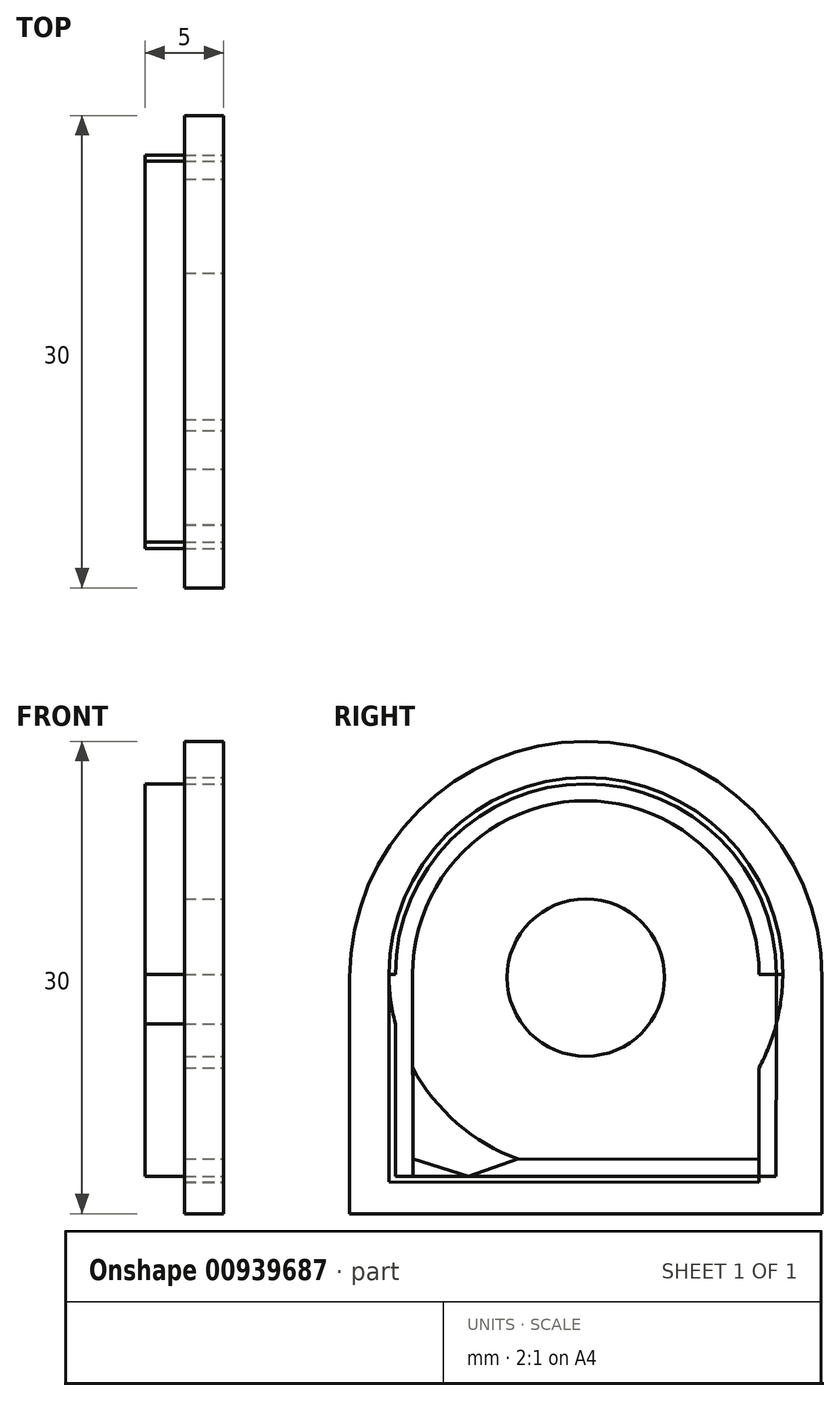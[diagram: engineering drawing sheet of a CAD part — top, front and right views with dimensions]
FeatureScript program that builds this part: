
annotation { "Feature Type Name" : "Feature", "Feature Type Description" : "" }
export const myFeature = defineFeature(function(context is Context, id is Id, definition is map)
    precondition{}
    {
        {
            var Q0;
            Q0=qCreatedBy(makeId("Right.planeOp"),FACE);
            var sketch = newSketch(context, id + "F0", { "sketchPlane" : qUnion([Q0])});
            skArc(sketch, "E0.0", {"start": v(-0.62, 5.76) * mm, "mid": v(-13.12, 18.27) * mm, "end": v(-25.63, 5.77) * mm});
            skArc(sketch, "E1.0", {"start": v(1.88, 5.56) * mm, "mid": v(-13.13, 20.56) * mm, "end": v(-28.12, 5.56) * mm});
            skLineSegment(sketch, "E2.0.0", {"start": v(-28.12, -9.44) * mm, "end": v(1.88, -9.44) * mm});
            skLineSegment(sketch, "E2.0.1", {"start": v(1.88, -9.44) * mm, "end": v(1.88, -4.44) * mm});
            skLineSegment(sketch, "E2.0.2", {"start": v(1.88, -4.44) * mm, "end": v(1.88, 5.56) * mm});
            skLineSegment(sketch, "E2.0.4", {"start": v(-28.12, 5.56) * mm, "end": v(-28.12, -9.44) * mm});
            skLineSegment(sketch, "E3.0", {"start": v(-25.63, 5.77) * mm, "end": v(-25.63, -7.44) * mm});
            skLineSegment(sketch, "E4.0", {"start": v(-25.63, -7.44) * mm, "end": v(-0.62, -7.44) * mm});
            skLineSegment(sketch, "E5.0", {"start": v(-0.62, 5.76) * mm, "end": v(-0.62, -7.44) * mm});
            skLineSegment(sketch, "E6.0.0", {"start": v(1.88, -9.44) * mm, "end": v(71.88, -9.44) * mm});
            skLineSegment(sketch, "E6.0.1", {"start": v(71.88, -9.44) * mm, "end": v(66.88, -4.44) * mm});
            skLineSegment(sketch, "E6.0.2", {"start": v(66.88, -4.44) * mm, "end": v(1.88, -4.44) * mm});
            skLineSegment(sketch, "E6.0.3", {"start": v(1.88, -4.44) * mm, "end": v(1.88, -9.44) * mm});
            skCircle(sketch, "E7", {"center": v(-13.12, 5.76) * mm, "radius": 12.5 * mm});
            skCircle(sketch, "E8", {"center": v(-13.12, 5.56) * mm, "radius": 5 * mm});
            skLineSegment(sketch, "E9", {"start": v(-25.63, 5.77) * mm, "end": v(-24.13, 5.77) * mm});
            skLineSegment(sketch, "E10", {"start": v(-0.62, 5.76) * mm, "end": v(-2.12, 5.76) * mm});
            skArc(sketch, "E11", {"start": v(-2.12, 5.76) * mm, "mid": v(-13.12, 16.79) * mm, "end": v(-24.13, 5.77) * mm});
            skLineSegment(sketch, "E12", {"start": v(-0.62, 5.76) * mm, "end": v(-1.02, 5.76) * mm});
            skLineSegment(sketch, "E13", {"start": v(-25.63, 5.77) * mm, "end": v(-25.23, 5.77) * mm});
            skArc(sketch, "E14", {"start": v(-1.02, 5.76) * mm, "mid": v(-13.12, 17.87) * mm, "end": v(-25.23, 5.77) * mm});
            skLineSegment(sketch, "E15", {"start": v(-25.23, 5.77) * mm, "end": v(-25.23, -7.44) * mm});
            skLineSegment(sketch, "E16", {"start": v(-24.13, 5.77) * mm, "end": v(-24.1, -7.44) * mm});
            skLineSegment(sketch, "E17", {"start": v(-2.12, 5.76) * mm, "end": v(-2.15, -7.44) * mm});
            skLineSegment(sketch, "E18", {"start": v(-1.02, 5.76) * mm, "end": v(-1.05, -7.44) * mm});
            skLineSegment(sketch, "E19", {"start": v(-1.05, -7.44) * mm, "end": v(-24.1, -7.44) * mm});
            skLineSegment(sketch, "E20", {"start": v(-24.1, -7.44) * mm, "end": v(-24.1, -7.04) * mm});
            skLineSegment(sketch, "E21", {"start": v(-2.15, -7.08) * mm, "end": v(-2.14, -5.98) * mm});
            skLineSegment(sketch, "E22", {"start": v(-2.14, -5.98) * mm, "end": v(-24.1, -5.97) * mm});
            skLineSegment(sketch, "E23", {"start": v(-24.1, -5.97) * mm, "end": v(-17.43, -5.97) * mm});
            skLineSegment(sketch, "E24", {"start": v(-8.83, -5.98) * mm, "end": v(-2.14, -5.98) * mm});
            skLineSegment(sketch, "E25", {"start": v(-2.15, -7.08) * mm, "end": v(-1.05, -7.08) * mm});
            skLineSegment(sketch, "E26", {"start": v(-1.05, -7.08) * mm, "end": v(-25.23, -7.07) * mm});
            skLineSegment(sketch, "E27", {"start": v(-17.43, -5.97) * mm, "end": v(-20.57, -7.07) * mm});
            skLineSegment(sketch, "E28", {"start": v(-20.57, -7.07) * mm, "end": v(-24.1, -5.97) * mm});
            skLineSegment(sketch, "E29", {"start": v(-24.1, -5.97) * mm, "end": v(-24.1, -7.04) * mm});
            skSolve(sketch);
        }
        {
            var Q0;
            Q0=makeQuery(id+"F0.imprint","IMPRINT",FACE,{"disambiguationData":[TD([[makeQuery(id+"F0.imprint","IMPRINT",EDGE,{"derivedFrom":sQuery(id+"F0.wireOp",EDGE,"E2.0.0")}),1.0]])]});
            var Q1;
            Q1=makeQuery(id+"F0.imprint","IMPRINT",FACE,{"disambiguationData":[TD([[makeQuery(id+"F0.imprint","IMPRINT",EDGE,{"derivedFrom":sQuery(id+"F0.wireOp",EDGE,"E8")}),-1.0]])]});
            var Q2;
            {var subQ0=sQuery(id+"F0.wireOp",EDGE,"E3.0");Q2=makeQuery(id+"F0.imprint","IMPRINT",FACE,{"disambiguationData":[TD([[makeQuery(id+"F0.imprint","IMPRINT",EDGE,{"derivedFrom":subQ0}),1.0]])]});}
            var Q3;
            Q3=makeQuery(id+"F0.imprint","IMPRINT",FACE,{"disambiguationData":[TD([[makeQuery(id+"F0.imprint","IMPRINT",EDGE,{"derivedFrom":sQuery(id+"F0.wireOp",EDGE,"E9")}),1.0]])]});
            var Q4;
            {var subQ0=sQuery(id+"F0.wireOp",EDGE,"E12");Q4=makeQuery(id+"F0.imprint","IMPRINT",FACE,{"disambiguationData":[TD([[makeQuery(id+"F0.imprint","IMPRINT",EDGE,{"derivedFrom":subQ0}),-1.0]])]});}
            var Q5;
            {var subQ2=sQuery(id+"F0.wireOp",EDGE,"E13");Q5=makeQuery(id+"F0.imprint","IMPRINT",FACE,{"disambiguationData":[TD([[makeQuery(id+"F0.imprint","IMPRINT",EDGE,{"derivedFrom":subQ2}),-1.0]])]});}
            var Q6;
            {var subQ5=sQuery(id+"F0.wireOp",EDGE,"E9");Q6=makeQuery(id+"F0.imprint","IMPRINT",FACE,{"disambiguationData":[TD([[makeQuery(id+"F0.imprint","IMPRINT",EDGE,{"derivedFrom":subQ5}),-1.0]])]});}
            var Q7;
            {var subQ0=sQuery(id+"F0.wireOp",EDGE,"E20");Q7=makeQuery(id+"F0.imprint","IMPRINT",FACE,{"disambiguationData":[TD([[makeQuery(id+"F0.imprint","IMPRINT",EDGE,{"derivedFrom":subQ0}),1.0]])]});}
            var Q8;
            {var subQ0=sQuery(id+"F0.wireOp",EDGE,"NrDhrhhL-rTPf-8MJP-CKrF-6Iw7iG4QOgd4");Q8=makeQuery(id+"F0.imprint","IMPRINT",FACE,{"disambiguationData":[TD([[makeQuery(id+"F0.imprint","IMPRINT",EDGE,{"derivedFrom":subQ0}),1.0]])]});}
            var Q9;
            {var subQ0=sQuery(id+"F0.wireOp",EDGE,"E22");var subQ1=sQuery(id+"F0.wireOp",EDGE,"E7");var subQ2=makeQuery(id+"F0.imprint","INTERSECT",VERTEX,{"disambiguationData":[OD(0.0)],"derivedFrom":[subQ1,subQ0]});Q9=makeQuery(id+"F0.imprint","IMPRINT",FACE,{"disambiguationData":[TD([[makeQuery(id+"F0.imprint","IMPRINT",EDGE,{"disambiguationData":[TD([[subQ2,-1.0]])],"derivedFrom":subQ1}),1.0]])]});}
            var Q10;
            {var subQ3=sQuery(id+"F0.wireOp",EDGE,"E20");Q10=makeQuery(id+"F0.imprint","IMPRINT",FACE,{"disambiguationData":[TD([[makeQuery(id+"F0.imprint","IMPRINT",EDGE,{"derivedFrom":subQ3}),-1.0]])]});}
            var Q11;
            {var subQ0=sQuery(id+"F0.wireOp",EDGE,"E5.0");Q11=makeQuery(id+"F0.imprint","IMPRINT",FACE,{"disambiguationData":[TD([[makeQuery(id+"F0.imprint","IMPRINT",EDGE,{"derivedFrom":subQ0}),-1.0]])]});}
            var Q12;
            {var subQ0=sQuery(id+"F0.wireOp",EDGE,"E12");Q12=makeQuery(id+"F0.imprint","IMPRINT",FACE,{"disambiguationData":[TD([[makeQuery(id+"F0.imprint","IMPRINT",EDGE,{"derivedFrom":subQ0}),1.0]])]});}
            var Q13;
            {var subQ5=sQuery(id+"F0.wireOp",EDGE,"E10");Q13=makeQuery(id+"F0.imprint","IMPRINT",FACE,{"disambiguationData":[TD([[makeQuery(id+"F0.imprint","IMPRINT",EDGE,{"derivedFrom":subQ5}),1.0]])]});}
            var Q14;
            {var subQ3=sQuery(id+"F0.wireOp",EDGE,"E7");var subQ5=sQuery(id+"F0.wireOp",EDGE,"E17");var subQ8=makeQuery(id+"F0.imprint","INTERSECT",VERTEX,{"derivedFrom":[subQ3,subQ5]});Q14=makeQuery(id+"F0.imprint","IMPRINT",FACE,{"disambiguationData":[TD([[makeQuery(id+"F0.imprint","IMPRINT",EDGE,{"disambiguationData":[TD([[subQ8,-1.0]])],"derivedFrom":subQ3}),-1.0]])]});}
            var Q15;
            {var subQ0=sQuery(id+"F0.wireOp",EDGE,"E22");var subQ1=sQuery(id+"F0.wireOp",EDGE,"E7");var subQ2=makeQuery(id+"F0.imprint","INTERSECT",VERTEX,{"disambiguationData":[OD(1.0)],"derivedFrom":[subQ1,subQ0]});Q15=makeQuery(id+"F0.imprint","IMPRINT",FACE,{"disambiguationData":[TD([[makeQuery(id+"F0.imprint","IMPRINT",EDGE,{"disambiguationData":[TD([[subQ2,-1.0]])],"derivedFrom":subQ1}),-1.0]])]});}
            var Q16;
            {var subQ5=sQuery(id+"F0.wireOp",EDGE,"E7");var subQ7=sQuery(id+"F0.wireOp",EDGE,"E15");var subQ9=makeQuery(id+"F0.imprint","INTERSECT",VERTEX,{"derivedFrom":[subQ5,subQ7]});Q16=makeQuery(id+"F0.imprint","IMPRINT",FACE,{"disambiguationData":[TD([[makeQuery(id+"F0.imprint","IMPRINT",EDGE,{"disambiguationData":[TD([[subQ9,-1.0]])],"derivedFrom":subQ5}),-1.0]])]});}
            var Q17;
            {var subQ0=sQuery(id+"F0.wireOp",EDGE,"E24");Q17=makeQuery(id+"F0.imprint","IMPRINT",FACE,{"disambiguationData":[TD([[makeQuery(id+"F0.imprint","IMPRINT",EDGE,{"derivedFrom":subQ0}),1.0]])]});}
            var Q18;
            {var subQ2=sQuery(id+"F0.wireOp",EDGE,"E17");var subQ5=sQuery(id+"F0.wireOp",EDGE,"E19");var subQ8=makeQuery(id+"F0.imprint","INTERSECT",VERTEX,{"derivedFrom":[subQ2,subQ5]});Q18=makeQuery(id+"F0.imprint","IMPRINT",FACE,{"disambiguationData":[TD([[makeQuery(id+"F0.imprint","IMPRINT",EDGE,{"disambiguationData":[TD([[subQ8,1.0]])],"derivedFrom":subQ2}),-1.0]])]});}
            var Q19;
            {var subQ0=sQuery(id+"F0.wireOp",EDGE,"E19");var subQ1=sQuery(id+"F0.wireOp",EDGE,"E17");var subQ2=makeQuery(id+"F0.imprint","INTERSECT",VERTEX,{"derivedFrom":[subQ1,subQ0]});Q19=makeQuery(id+"F0.imprint","IMPRINT",FACE,{"disambiguationData":[TD([[makeQuery(id+"F0.imprint","IMPRINT",EDGE,{"disambiguationData":[TD([[subQ2,1.0]])],"derivedFrom":subQ1}),1.0]])]});}
            var Q20;
            {var subQ0=sQuery(id+"F0.wireOp",EDGE,"E23");Q20=makeQuery(id+"F0.imprint","IMPRINT",FACE,{"disambiguationData":[TD([[makeQuery(id+"F0.imprint","IMPRINT",EDGE,{"derivedFrom":subQ0}),1.0]])]});}
            var Q21;
            Q21=makeQuery(id+"F0.imprint","IMPRINT",FACE,{"disambiguationData":[TD([[makeQuery(id+"F0.imprint","IMPRINT",EDGE,{"derivedFrom":sQuery(id+"F0.wireOp",EDGE,"E23")}),-1.0]])]});
            var Q22;
            {var subQ1=sQuery(id+"F0.wireOp",EDGE,"E21");Q22=makeQuery(id+"F0.imprint","IMPRINT",FACE,{"disambiguationData":[TD([[makeQuery(id+"F0.imprint","IMPRINT",EDGE,{"derivedFrom":subQ1}),1.0]])]});}
            var Q23;
            {var subQ0=sQuery(id+"F0.wireOp",EDGE,"E22");Q23=makeQuery(id+"F0.imprint","IMPRINT",FACE,{"disambiguationData":[TD([[makeQuery(id+"F0.imprint","IMPRINT",EDGE,{"derivedFrom":subQ0}),1.0]])]});}
            extrude(context, id + "F1", {"entities" : qUnion([Q0, Q1, Q2, Q3, Q4, Q5, Q6, Q7, Q8, Q9, Q10, Q11, Q12, Q13, Q14, Q15, Q16, Q17, Q18, Q19, Q20, Q21, Q22, Q23]), "oppositeDirection" : true, "depth" : 2.5 * mm, "offsetDistance" : 25 * mm});
        }
        {
            var Q0;
            {var subQ5=sQuery(id+"F0.wireOp",EDGE,"E9");Q0=makeQuery(id+"F0.imprint","IMPRINT",FACE,{"disambiguationData":[TD([[makeQuery(id+"F0.imprint","IMPRINT",EDGE,{"derivedFrom":subQ5}),-1.0]])]});}
            var Q1;
            Q1=makeQuery(id+"F0.imprint","IMPRINT",FACE,{"disambiguationData":[TD([[makeQuery(id+"F0.imprint","IMPRINT",EDGE,{"derivedFrom":sQuery(id+"F0.wireOp",EDGE,"E9")}),1.0]])]});
            var Q2;
            {var subQ5=sQuery(id+"F0.wireOp",EDGE,"E10");Q2=makeQuery(id+"F0.imprint","IMPRINT",FACE,{"disambiguationData":[TD([[makeQuery(id+"F0.imprint","IMPRINT",EDGE,{"derivedFrom":subQ5}),1.0]])]});}
            var Q3;
            {var subQ3=sQuery(id+"F0.wireOp",EDGE,"E7");var subQ5=sQuery(id+"F0.wireOp",EDGE,"E17");var subQ8=makeQuery(id+"F0.imprint","INTERSECT",VERTEX,{"derivedFrom":[subQ3,subQ5]});Q3=makeQuery(id+"F0.imprint","IMPRINT",FACE,{"disambiguationData":[TD([[makeQuery(id+"F0.imprint","IMPRINT",EDGE,{"disambiguationData":[TD([[subQ8,-1.0]])],"derivedFrom":subQ3}),-1.0]])]});}
            var Q4;
            {var subQ0=sQuery(id+"F0.wireOp",EDGE,"E22");Q4=makeQuery(id+"F0.imprint","IMPRINT",FACE,{"disambiguationData":[TD([[makeQuery(id+"F0.imprint","IMPRINT",EDGE,{"derivedFrom":subQ0}),1.0]])]});}
            var Q5;
            {var subQ5=sQuery(id+"F0.wireOp",EDGE,"E7");var subQ7=sQuery(id+"F0.wireOp",EDGE,"E15");var subQ9=makeQuery(id+"F0.imprint","INTERSECT",VERTEX,{"derivedFrom":[subQ5,subQ7]});Q5=makeQuery(id+"F0.imprint","IMPRINT",FACE,{"disambiguationData":[TD([[makeQuery(id+"F0.imprint","IMPRINT",EDGE,{"disambiguationData":[TD([[subQ9,-1.0]])],"derivedFrom":subQ5}),-1.0]])]});}
            var Q6;
            Q6=makeQuery(id+"F0.imprint","IMPRINT",FACE,{"disambiguationData":[TD([[makeQuery(id+"F0.imprint","IMPRINT",EDGE,{"derivedFrom":sQuery(id+"F0.wireOp",EDGE,"E23")}),-1.0]])]});
            var Q7;
            {var subQ1=sQuery(id+"F0.wireOp",EDGE,"E21");Q7=makeQuery(id+"F0.imprint","IMPRINT",FACE,{"disambiguationData":[TD([[makeQuery(id+"F0.imprint","IMPRINT",EDGE,{"derivedFrom":subQ1}),1.0]])]});}
            extrude(context, id + "F2", {"entities" : qUnion([Q0, Q1, Q2, Q3, Q4, Q5, Q6, Q7]), "oppositeDirection" : true, "depth" : 5 * mm, "offsetDistance" : 25 * mm});
        }
        {
            var Q0;
            {var subQ4=sQuery(id+"F0.wireOp",EDGE,"E28");Q0=makeQuery(id+"F0.imprint","IMPRINT",FACE,{"disambiguationData":[TD([[makeQuery(id+"F0.imprint","IMPRINT",EDGE,{"derivedFrom":subQ4}),1.0]])]});}
            extrude(context, id + "F3", {"entities" : qUnion([Q0]), "oppositeDirection" : true, "depth" : 5 * mm, "offsetDistance" : 25 * mm});
        }
    });
